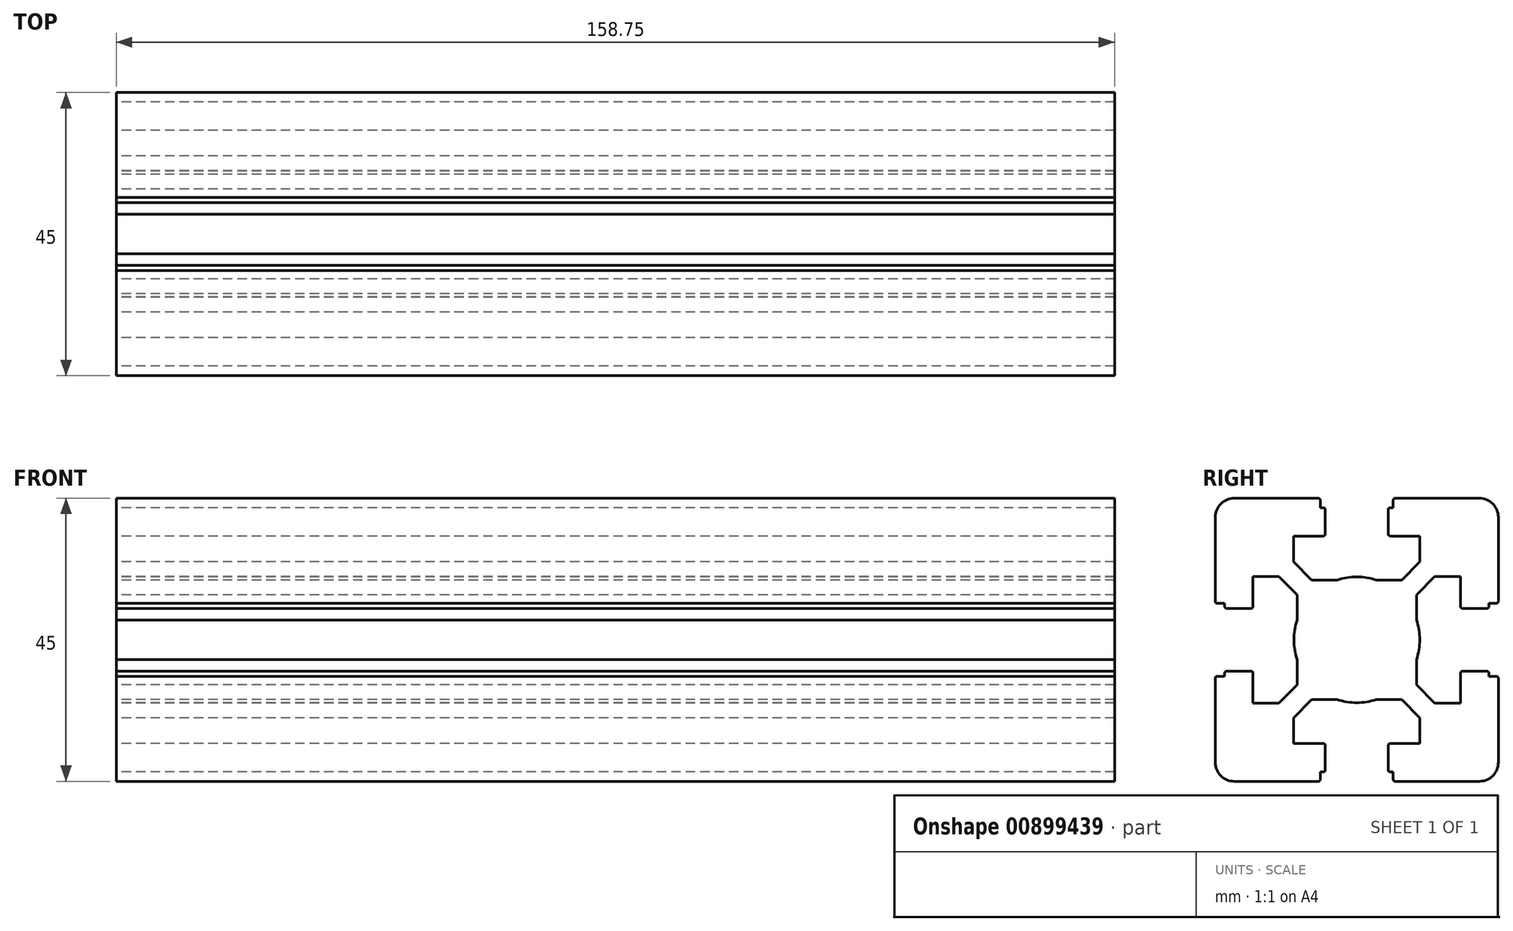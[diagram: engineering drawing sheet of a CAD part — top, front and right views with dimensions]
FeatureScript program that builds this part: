
annotation { "Feature Type Name" : "Feature", "Feature Type Description" : "" }
export const myFeature = defineFeature(function(context is Context, id is Id, definition is map)
    precondition{}
    {
        {
            var Q0;
            Q0=qCreatedBy(makeId("Right.planeOp"),FACE);
            var sketch = newSketch(context, id + "F0", { "sketchPlane" : qUnion([Q0])});
            skLineSegment(sketch, "E0", {"start": v(-20.09, -10.29) * mm, "end": v(-21.29, -10.29) * mm});
            skArc(sketch, "E1", {"start": v(-21.29, -10.29) * mm, "mid": v(-21.5, -10.38) * mm, "end": v(-21.59, -10.59) * mm});
            skLineSegment(sketch, "E2", {"start": v(-21.59, -10.59) * mm, "end": v(-21.59, -23.99) * mm});
            skArc(sketch, "E3", {"start": v(-21.59, -23.99) * mm, "mid": v(-20.7, -26.11) * mm, "end": v(-18.59, -26.99) * mm});
            skLineSegment(sketch, "E4", {"start": v(-18.59, -26.99) * mm, "end": v(-5.19, -26.99) * mm});
            skArc(sketch, "E5", {"start": v(-5.19, -26.99) * mm, "mid": v(-4.98, -26.9) * mm, "end": v(-4.89, -26.69) * mm});
            skLineSegment(sketch, "E6", {"start": v(-4.89, -26.69) * mm, "end": v(-4.89, -25.49) * mm});
            skLineSegment(sketch, "E7", {"start": v(-4.89, -25.49) * mm, "end": v(-4.39, -25.49) * mm});
            skArc(sketch, "E8", {"start": v(-4.39, -25.49) * mm, "mid": v(-4.18, -25.4) * mm, "end": v(-4.09, -25.19) * mm});
            skLineSegment(sketch, "E9", {"start": v(-4.09, -25.19) * mm, "end": v(-4.09, -21.29) * mm});
            skArc(sketch, "E10", {"start": v(-4.09, -21.29) * mm, "mid": v(-4.18, -21.08) * mm, "end": v(-4.39, -20.99) * mm});
            skLineSegment(sketch, "E11", {"start": v(-4.39, -20.99) * mm, "end": v(-9.14, -20.99) * mm});
            skLineSegment(sketch, "E12", {"start": v(-9.14, -20.99) * mm, "end": v(-9.14, -16.88) * mm});
            skLineSegment(sketch, "E13", {"start": v(-9.14, -16.88) * mm, "end": v(-6.25, -13.99) * mm});
            skLineSegment(sketch, "E14", {"start": v(-6.25, -13.99) * mm, "end": v(-2.21, -13.99) * mm});
            skArc(sketch, "E15", {"start": v(-2.21, -13.99) * mm, "mid": v(0.91, -14.49) * mm, "end": v(4.03, -13.99) * mm});
            skLineSegment(sketch, "E16", {"start": v(-20.09, -10.29) * mm, "end": v(-20.09, -9.79) * mm});
            skArc(sketch, "E17", {"start": v(-20.09, -9.79) * mm, "mid": v(-20, -9.58) * mm, "end": v(-19.79, -9.49) * mm});
            skLineSegment(sketch, "E18", {"start": v(-19.79, -9.49) * mm, "end": v(-15.89, -9.49) * mm});
            skArc(sketch, "E19", {"start": v(-15.89, -9.49) * mm, "mid": v(-15.68, -9.58) * mm, "end": v(-15.59, -9.79) * mm});
            skLineSegment(sketch, "E20", {"start": v(-15.59, -9.79) * mm, "end": v(-15.59, -14.54) * mm});
            skLineSegment(sketch, "E21", {"start": v(-15.59, -14.54) * mm, "end": v(-11.48, -14.54) * mm});
            skLineSegment(sketch, "E22", {"start": v(-11.48, -14.54) * mm, "end": v(-8.59, -11.65) * mm});
            skLineSegment(sketch, "E23", {"start": v(-8.59, -11.65) * mm, "end": v(-8.59, -7.61) * mm});
            skLineSegment(sketch, "E24", {"start": v(29.82, -4.49) * mm, "end": v(-31.05, -4.49) * mm});
            skLineSegment(sketch, "E25.MirrorCS", {"start": v(6.71, -25.49) * mm, "end": v(6.21, -25.49) * mm});
            skArc(sketch, "E26.MirrorCS", {"start": v(7.01, -26.99) * mm, "mid": v(6.8, -26.9) * mm, "end": v(6.71, -26.69) * mm});
            skLineSegment(sketch, "E27.MirrorCS", {"start": v(10.41, -11.65) * mm, "end": v(10.41, -7.61) * mm});
            skArc(sketch, "E28.MirrorCS", {"start": v(6.21, -25.49) * mm, "mid": v(6, -25.4) * mm, "end": v(5.91, -25.19) * mm});
            skLineSegment(sketch, "E29.MirrorCS", {"start": v(6.71, -26.69) * mm, "end": v(6.71, -25.49) * mm});
            skArc(sketch, "E30.MirrorCS", {"start": v(5.91, -21.29) * mm, "mid": v(6, -21.08) * mm, "end": v(6.21, -20.99) * mm});
            skLineSegment(sketch, "E31.MirrorCS", {"start": v(10.96, -16.88) * mm, "end": v(8.07, -13.99) * mm});
            skLineSegment(sketch, "E32.MirrorCS", {"start": v(13.3, -14.54) * mm, "end": v(10.41, -11.65) * mm});
            skLineSegment(sketch, "E33.MirrorCS", {"start": v(17.41, -14.54) * mm, "end": v(13.3, -14.54) * mm});
            skLineSegment(sketch, "E34.MirrorCS", {"start": v(17.41, -9.79) * mm, "end": v(17.41, -14.54) * mm});
            skLineSegment(sketch, "E35.MirrorCS", {"start": v(6.21, -20.99) * mm, "end": v(10.96, -20.99) * mm});
            skLineSegment(sketch, "E36.MirrorCS", {"start": v(8.07, -13.99) * mm, "end": v(4.03, -13.99) * mm});
            skArc(sketch, "E37.MirrorCS", {"start": v(4.03, -13.99) * mm, "mid": v(0.91, -14.49) * mm, "end": v(-2.21, -13.99) * mm});
            skLineSegment(sketch, "E38.MirrorCS", {"start": v(10.96, -20.99) * mm, "end": v(10.96, -16.88) * mm});
            skLineSegment(sketch, "E39.MirrorCS", {"start": v(5.91, -25.19) * mm, "end": v(5.91, -21.29) * mm});
            skArc(sketch, "E40.MirrorCS", {"start": v(23.41, -23.99) * mm, "mid": v(22.53, -26.11) * mm, "end": v(20.41, -26.99) * mm});
            skLineSegment(sketch, "E41.MirrorCS", {"start": v(20.41, -26.99) * mm, "end": v(7.01, -26.99) * mm});
            skLineSegment(sketch, "E42.MirrorCS", {"start": v(23.41, -10.59) * mm, "end": v(23.41, -23.99) * mm});
            skArc(sketch, "E43.MirrorCS", {"start": v(17.71, -9.49) * mm, "mid": v(17.5, -9.58) * mm, "end": v(17.41, -9.79) * mm});
            skArc(sketch, "E44.MirrorCS", {"start": v(23.11, -10.29) * mm, "mid": v(23.32, -10.38) * mm, "end": v(23.41, -10.59) * mm});
            skLineSegment(sketch, "E45.MirrorCS", {"start": v(21.91, -10.29) * mm, "end": v(21.91, -9.79) * mm});
            skLineSegment(sketch, "E46.MirrorCS", {"start": v(21.91, -10.29) * mm, "end": v(23.11, -10.29) * mm});
            skArc(sketch, "E47.MirrorCS", {"start": v(21.91, -9.79) * mm, "mid": v(21.82, -9.58) * mm, "end": v(21.61, -9.49) * mm});
            skLineSegment(sketch, "E48.MirrorCS", {"start": v(21.61, -9.49) * mm, "end": v(17.71, -9.49) * mm});
            skLineSegment(sketch, "E49.MirrorCS", {"start": v(6.71, 16.51) * mm, "end": v(6.21, 16.51) * mm});
            skArc(sketch, "E50.MirrorCS", {"start": v(-4.39, 16.51) * mm, "mid": v(-4.18, 16.42) * mm, "end": v(-4.09, 16.21) * mm});
            skLineSegment(sketch, "E51.MirrorCS", {"start": v(-4.89, 16.51) * mm, "end": v(-4.39, 16.51) * mm});
            skArc(sketch, "E52.MirrorCS", {"start": v(5.91, 12.31) * mm, "mid": v(6, 12.1) * mm, "end": v(6.21, 12.01) * mm});
            skLineSegment(sketch, "E53.MirrorCS", {"start": v(6.71, 17.71) * mm, "end": v(6.71, 16.51) * mm});
            skLineSegment(sketch, "E54.MirrorCS", {"start": v(-4.89, 17.71) * mm, "end": v(-4.89, 16.51) * mm});
            skArc(sketch, "E55.MirrorCS", {"start": v(-5.19, 18.01) * mm, "mid": v(-4.98, 17.92) * mm, "end": v(-4.89, 17.71) * mm});
            skArc(sketch, "E56.MirrorCS", {"start": v(-4.09, 12.31) * mm, "mid": v(-4.18, 12.1) * mm, "end": v(-4.39, 12.01) * mm});
            skArc(sketch, "E57.MirrorCS", {"start": v(7.01, 18.01) * mm, "mid": v(6.8, 17.92) * mm, "end": v(6.71, 17.71) * mm});
            skArc(sketch, "E58.MirrorCS", {"start": v(6.21, 16.51) * mm, "mid": v(6, 16.42) * mm, "end": v(5.91, 16.21) * mm});
            skArc(sketch, "E59.MirrorCS", {"start": v(23.11, 1.31) * mm, "mid": v(23.32, 1.4) * mm, "end": v(23.41, 1.61) * mm});
            skLineSegment(sketch, "E60.MirrorCS", {"start": v(21.91, 1.31) * mm, "end": v(21.91, 0.81) * mm});
            skArc(sketch, "E61.MirrorCS", {"start": v(-15.89, 0.51) * mm, "mid": v(-15.68, 0.6) * mm, "end": v(-15.59, 0.81) * mm});
            skArc(sketch, "E62.MirrorCS", {"start": v(-21.29, 1.31) * mm, "mid": v(-21.5, 1.4) * mm, "end": v(-21.59, 1.61) * mm});
            skArc(sketch, "E63.MirrorCS", {"start": v(17.71, 0.51) * mm, "mid": v(17.5, 0.6) * mm, "end": v(17.41, 0.81) * mm});
            skArc(sketch, "E64.MirrorCS", {"start": v(21.91, 0.81) * mm, "mid": v(21.82, 0.6) * mm, "end": v(21.61, 0.51) * mm});
            skLineSegment(sketch, "E65.MirrorCS", {"start": v(21.91, 1.31) * mm, "end": v(23.11, 1.31) * mm});
            skArc(sketch, "E66.MirrorCS", {"start": v(14.31, 5.31) * mm, "mid": v(14.1, 5.4) * mm, "end": v(14.01, 5.61) * mm});
            skArc(sketch, "E67.MirrorCS", {"start": v(-20.09, 0.81) * mm, "mid": v(-20, 0.6) * mm, "end": v(-19.79, 0.51) * mm});
            skLineSegment(sketch, "E68.MirrorCS", {"start": v(-20.09, 1.31) * mm, "end": v(-21.29, 1.31) * mm});
            skLineSegment(sketch, "E69.MirrorCS", {"start": v(-20.09, 1.31) * mm, "end": v(-20.09, 0.81) * mm});
            skLineSegment(sketch, "E70.MirrorCS", {"start": v(8.07, 5.01) * mm, "end": v(4.03, 5.01) * mm});
            skLineSegment(sketch, "E71.MirrorCS", {"start": v(-4.09, 16.21) * mm, "end": v(-4.09, 12.31) * mm});
            skLineSegment(sketch, "E72.MirrorCS", {"start": v(-9.14, 12.01) * mm, "end": v(-9.14, 7.9) * mm});
            skLineSegment(sketch, "E73.MirrorCS", {"start": v(-15.59, 5.56) * mm, "end": v(-11.48, 5.56) * mm});
            skLineSegment(sketch, "E74.MirrorCS", {"start": v(-4.39, 12.01) * mm, "end": v(-9.14, 12.01) * mm});
            skLineSegment(sketch, "E75.MirrorCS", {"start": v(-9.14, 7.9) * mm, "end": v(-6.25, 5.01) * mm});
            skLineSegment(sketch, "E76.MirrorCS", {"start": v(10.96, 12.01) * mm, "end": v(10.96, 7.9) * mm});
            skArc(sketch, "E77.MirrorCS", {"start": v(-21.59, 15.01) * mm, "mid": v(-20.7, 17.13) * mm, "end": v(-18.59, 18.01) * mm});
            skLineSegment(sketch, "E78.MirrorCS", {"start": v(23.41, 1.61) * mm, "end": v(23.41, 15.01) * mm});
            skLineSegment(sketch, "E79.MirrorCS", {"start": v(13.3, 5.56) * mm, "end": v(10.41, 2.67) * mm});
            skLineSegment(sketch, "E80.MirrorCS", {"start": v(-8.59, 2.67) * mm, "end": v(-8.59, -1.37) * mm});
            skLineSegment(sketch, "E81.MirrorCS", {"start": v(-15.59, 0.81) * mm, "end": v(-15.59, 5.56) * mm});
            skLineSegment(sketch, "E82.MirrorCS", {"start": v(10.41, 2.67) * mm, "end": v(10.41, -1.37) * mm});
            skLineSegment(sketch, "E83.MirrorCS", {"start": v(-18.59, 18.01) * mm, "end": v(-5.19, 18.01) * mm});
            skLineSegment(sketch, "E84.MirrorCS", {"start": v(10.96, 7.9) * mm, "end": v(8.07, 5.01) * mm});
            skLineSegment(sketch, "E85.MirrorCS", {"start": v(17.41, 5.56) * mm, "end": v(13.3, 5.56) * mm});
            skArc(sketch, "E86.MirrorCS", {"start": v(23.41, 15.01) * mm, "mid": v(22.53, 17.13) * mm, "end": v(20.41, 18.01) * mm});
            skLineSegment(sketch, "E87.MirrorCS", {"start": v(5.91, 16.21) * mm, "end": v(5.91, 12.31) * mm});
            skLineSegment(sketch, "E88.MirrorCS", {"start": v(17.41, 0.81) * mm, "end": v(17.41, 5.56) * mm});
            skLineSegment(sketch, "E89.MirrorCS", {"start": v(-11.48, 5.56) * mm, "end": v(-8.59, 2.67) * mm});
            skLineSegment(sketch, "E90.MirrorCS", {"start": v(-6.25, 5.01) * mm, "end": v(-2.21, 5.01) * mm});
            skLineSegment(sketch, "E91.MirrorCS", {"start": v(-21.59, 1.61) * mm, "end": v(-21.59, 15.01) * mm});
            skArc(sketch, "E92.MirrorCS", {"start": v(4.03, 5.01) * mm, "mid": v(0.91, 5.51) * mm, "end": v(-2.21, 5.01) * mm});
            skLineSegment(sketch, "E93.MirrorCS", {"start": v(6.21, 12.01) * mm, "end": v(10.96, 12.01) * mm});
            skArc(sketch, "E94.MirrorCS", {"start": v(-2.21, 5.01) * mm, "mid": v(0.91, 5.51) * mm, "end": v(4.03, 5.01) * mm});
            skLineSegment(sketch, "E95.MirrorCS", {"start": v(20.41, 18.01) * mm, "end": v(7.01, 18.01) * mm});
            skLineSegment(sketch, "E96.MirrorCS", {"start": v(-19.79, 0.51) * mm, "end": v(-15.89, 0.51) * mm});
            skLineSegment(sketch, "E97.MirrorCS", {"start": v(21.61, 0.51) * mm, "end": v(17.71, 0.51) * mm});
            skLineSegment(sketch, "E98.MirrorCS", {"start": v(0.91, -27.65) * mm, "end": v(0.91, 19.82) * mm});
            skArc(sketch, "E99", {"start": v(-8.59, -1.37) * mm, "mid": v(-9.09, -4.49) * mm, "end": v(-8.59, -7.61) * mm});
            skArc(sketch, "E100", {"start": v(10.41, -7.61) * mm, "mid": v(10.91, -4.49) * mm, "end": v(10.41, -1.37) * mm});
            skSolve(sketch);
        }
        {
            var Q0;
            Q0=qSketchRegion(id+"F0",true);
            extrude(context, id + "F1", {"entities" : qUnion([Q0]), "depth" : 158.75 * mm, "offsetDistance" : 25.4 * mm});
        }
    });
